# Revit family: QF_ELECTROLUXPROFESSIONAL_586061_PBOT15TGCO
name_source: partatom
category: Specialty Equipment
revit_build: Autodesk Revit 2018 (Build: 20190510_1515(x64)
units: mm (PartAtom-declared; Revit-internal decimal feet)

## family parameters
Always vertical = Yes
Cut with Voids When Loaded = No
Part Type = Normal
Room Calculation Point = No
Round Connector Dimension = Use Radius
Shared = Yes
Work Plane-Based = No

## types (1)
- 586061_STEAM BOILING PAN_ELECT._TILTING_150LT_(S)_FS
    50 Hertz Option = No
    60 Hertz Option = Yes
    Apparent Power = 0 VA
    Base Height = 100 mm  [stored 0.328084 ft]
    Cold Water Connection Height = 395 mm  [stored 1.29593 ft]
    Cold Water Radius Size = 6 mm  [stored 0.019685 ft]
    Cold Water Size = 1"
    Condensate Return Connection Height = 340 mm  [stored 1.11549 ft]
    Condensate Return Raduis  Size = 13 mm
    Condensate Return Size = 1"
    Conn Conduit = Yes
    Cycle = 60 Hz
    Depth = 900 mm  [stored 2.95276 ft]
    Description = High Productivity Cooking Steam Tilting Boiling Pan-150lt Freestanding-Hygienic Profile - Manual
    Direct Waste Size = 0"
    Elec Conn Connection Height = 450 mm  [stored 1.47638 ft]
    Electrical Remarks = 1PH+N 50/60HZ COMPATIBLE
    FL Amps = 0 A
    HP = 0.3 HP
    Height = 900 mm  [stored 2.95276 ft]
    Hot Water Connection Height = 395 mm  [stored 1.29593 ft]
    Hot Water Flow = 0 GPM
    Hot Water Radius Size = 6 mm  [stored 0.019685 ft]
    Hot Water Size = 1"
    Indirect Waste Connection Height = 0 mm  [stored 0 ft]
    Indirect Waste Radius Size = 0 mm  [stored 0 ft]
    Indirect Waste Size = 0"
    Manufacturer = ELECTROLUX
    Max Overcurrent Protection = 5 A
    Min Ckt Ampacity = 0 A
    Model = 586061
    Phase = 1
    Plumbing Remarks = For Domestic Water Connection
    Steam Consumption per Hour = 65
    Steam Supply Pressure = 21.76 psi
    Steam Supply Raduis Size = 13 mm
    Steam Supply Size = 1"
    Steam Supply Volume = 0 GPM
    URL = www.electrolux.com/foodservice
    URL Cutsheet = www.electrolux.com/foodservice
    URL Manufacturer = www.electrolux.com/foodservice
    Vessel Depth = 465 mm  [stored 1.52559 ft]
    Vessel Diameter = 710 mm
    Volts = 230 V
    Watts = 0 W
    Weight = 260 kg.
    Width = 1300 mm  [stored 4.26509 ft]

note: [stored X ft] marks values corroborated as IEEE doubles in the binary element streams (Revit-internal decimal feet)

## geometry (parser evidence)
native form markers: Blend x27, Sweep x5
no freeform markers — native parametric forms only
